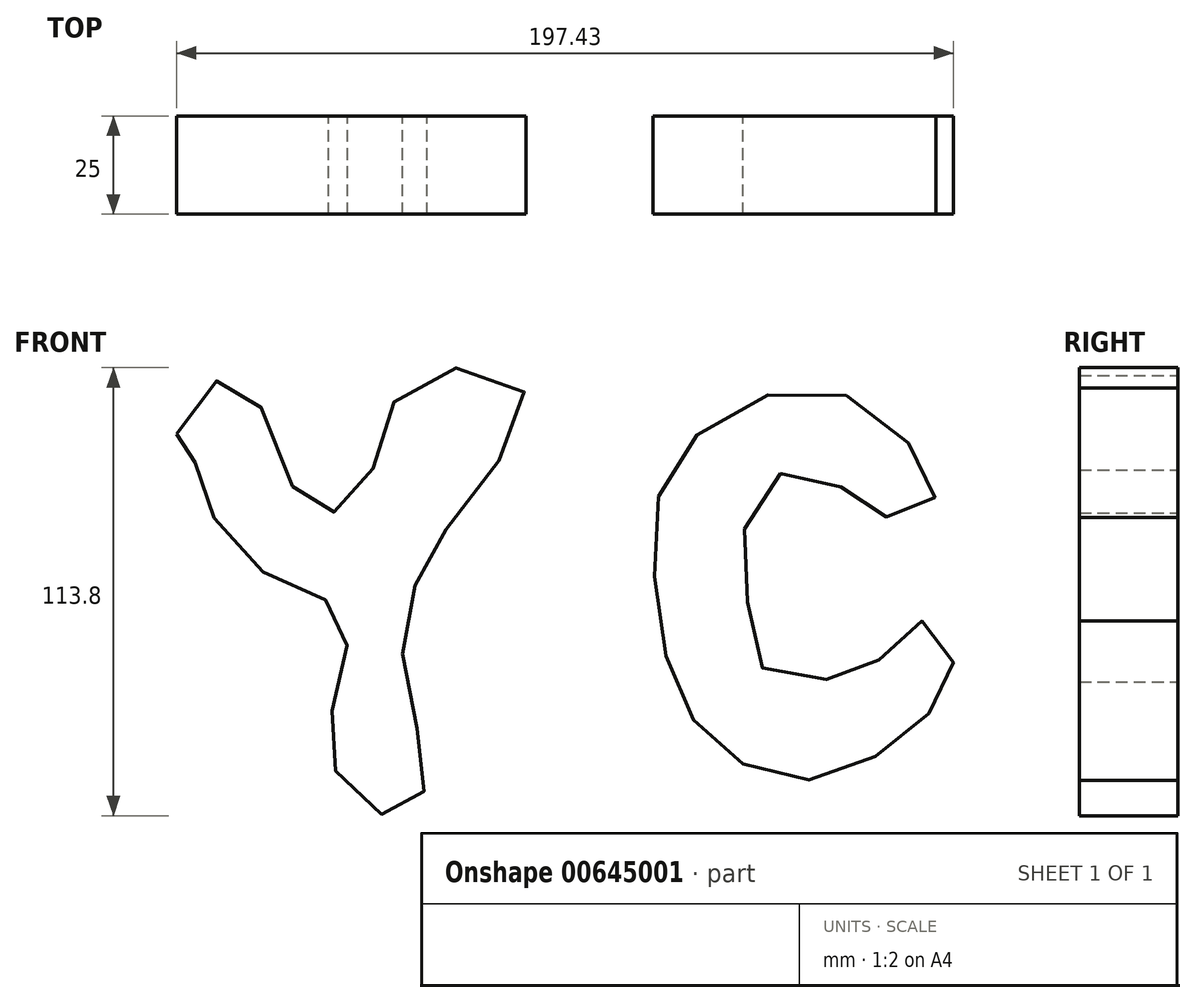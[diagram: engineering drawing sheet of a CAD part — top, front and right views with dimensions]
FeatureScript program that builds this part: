
annotation { "Feature Type Name" : "Feature", "Feature Type Description" : "" }
export const myFeature = defineFeature(function(context is Context, id is Id, definition is map)
    precondition{}
    {
        {
            var Q0;
            Q0=qCreatedBy(makeId("Front.planeOp"),FACE);
            var sketch = newSketch(context, id + "F0", { "sketchPlane" : qUnion([Q0])});
            skFitSpline(sketch, "E0", {"points": [v(-137.98, 52.42) * mm, v(-123.68, 67.17) * mm, v(-110.26, 42.59) * mm, v(-99.09, 32.3) * mm, v(-87.47, 44.82) * mm, v(-77.63, 66.28) * mm, v(-49.92, 63.6) * mm, v(-64.22, 34.99) * mm, v(-77.19, 14.42) * mm, v(-79.87, -11.5) * mm, v(-74.5, -36.54) * mm, v(-83.9, -44.59) * mm, v(-98.2, -31.62) * mm, v(-96.85, -11.95) * mm, v(-95.96, 6.82) * mm, v(-114.29, 16.21) * mm, v(-130.83, 36.33) * mm, v(-134.85, 48.4) * mm, v(-137.98, 52.42) * mm]});
            skSolve(sketch);
        }
        {
            var Q0;
            Q0=makeQuery(id+"F0.imprint","IMPRINT",FACE,{"disambiguationData":[TD([[makeQuery(id+"F0.imprint","IMPRINT",EDGE,{"derivedFrom":sQuery(id+"F0.wireOp",EDGE,"E0")}),-1.0]])]});
            extrude(context, id + "F1", {"entities" : qUnion([Q0]), "depth" : 25 * mm, "offsetDistance" : 25 * mm});
        }
        {
            var Q0;
            Q0=qCreatedBy(makeId("Front.planeOp"),FACE);
            var sketch = newSketch(context, id + "F2", { "sketchPlane" : qUnion([Q0])});
            skFitSpline(sketch, "E1", {"points": [v(48.03, 50.12) * mm, v(26.85, 63.71) * mm, v(0, 56.44) * mm, v(-14.87, 38.74) * mm, v(-16.14, 11.87) * mm, v(-10.76, -12.78) * mm, v(0, -27.32) * mm, v(18, -35.54) * mm, v(37.92, -30.48) * mm, v(53.72, -18.15) * mm, v(59.4, -5.83) * mm, v(52.46, 4.92) * mm, v(42.02, -3.61) * mm, v(32.23, -8.99) * mm, v(12.63, -8.67) * mm, v(7.25, 8.08) * mm, v(6.94, 30.52) * mm, v(18.32, 43.17) * mm, v(34.44, 36.21) * mm, v(43.6, 31.16) * mm, v(54.67, 36.21) * mm, v(48.03, 50.12) * mm]});
            skSolve(sketch);
        }
        {
            var Q0;
            Q0 = qSketchRegion(id + "F2", true);
            extrude(context, id + "F3", {"entities" : qUnion([Q0]), "depth" : 25 * mm, "offsetDistance" : 25 * mm});
        }
    });
